# Revit family: Construction_Roof-Accessories_Alpine-SnowGuards_SnowMax-Membrane-1.5
name_source: partatom
category: Specialty Equipment
units: mm (PartAtom-declared; Revit-internal decimal feet)

## family parameters
Cut with Voids When Loaded = No
Host = Face
OmniClass Number = 23.35.20.31.27.14
OmniClass Title = Snow Guards
Part Type = Normal
Room Calculation Point = No
Round Connector Dimension = Use Diameter
Shared = No

## types (1)
- SnowMax - Membrane 1.5
    Assembly Code = B3010
    Base Material = Alpine SnowGuards - Aluminium - Mill Finish
    Default Elevation = 48"
    Description = SnowMax Membrane bar-style snow guard bracket. 1.5'' wide bracket (fits décor ribs up to 1.5'' tall). 6''X5.5'' stainless steel base plate.
    Edition number = 1
    Horizontal Spacing = 20"
    Keynote = 07720
    Manufacturer = Alpine SnowGuards
    Model = SnowMax - Membrane 1.5
    Pad Material = Alpine SnowGuards - Aluminium - Mill Finish
    Patch Material = Alpine SnowGuards - Aluminium - Mill Finish
    Product Guid = 21c5dea5-83cb-4f32-afa3-5957870a91b9
    Product Material = Alpine SnowGuards - Aluminium - Mill Finish
    Product data url = https://www.bimobject.com
    URL = https://www.alpinesnowguards.com

## geometry (parser evidence)
native form markers: Sweep x6
no freeform markers — native parametric forms only
